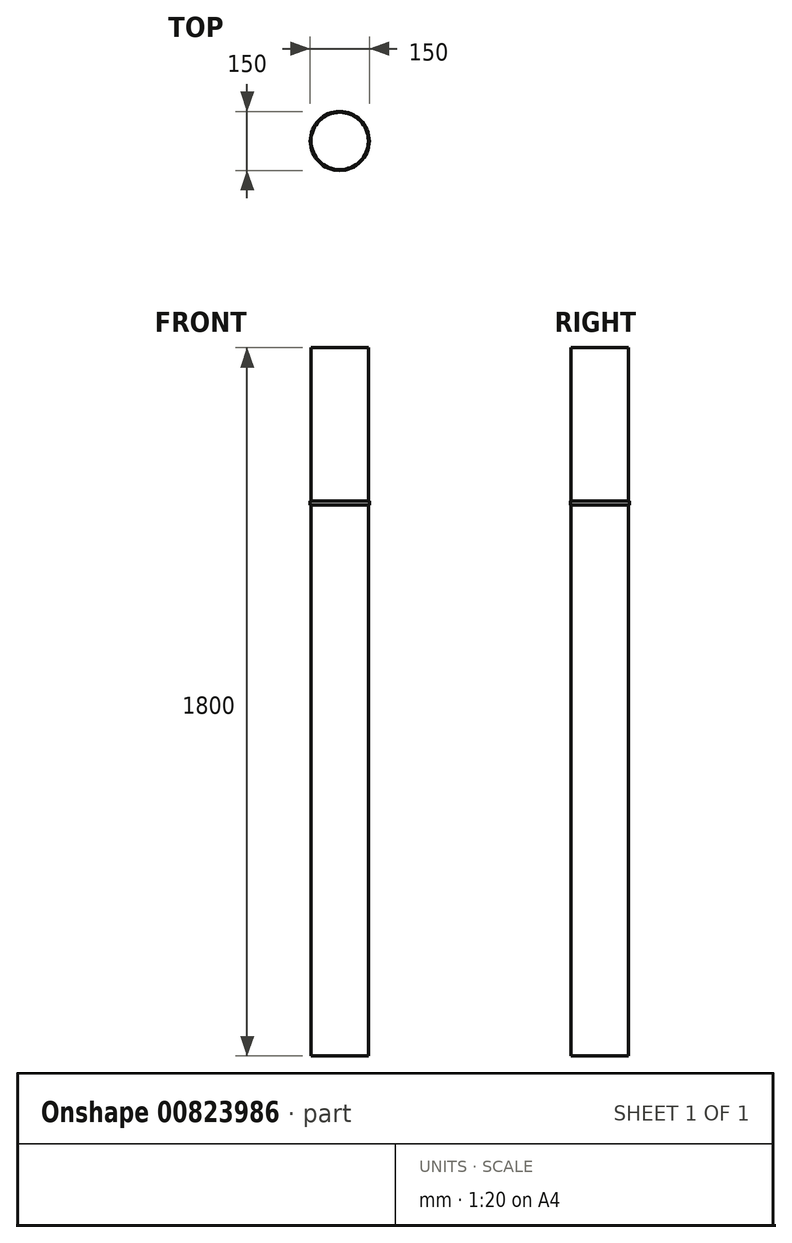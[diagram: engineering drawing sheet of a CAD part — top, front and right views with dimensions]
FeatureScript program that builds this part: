
annotation { "Feature Type Name" : "Feature", "Feature Type Description" : "" }
export const myFeature = defineFeature(function(context is Context, id is Id, definition is map)
    precondition{}
    {
        {
            var Q0;
            Q0=qCreatedBy(makeId("Top.planeOp"),FACE);
            var sketch = newSketch(context, id + "F0", { "sketchPlane" : qUnion([Q0])});
            skCircle(sketch, "E0", {"center": v(0, 0) * mm, "radius": 72.78 * mm});
            skSolve(sketch);
        }
        {
            var Q0;
            Q0=makeQuery(id+"F0.imprint","IMPRINT",FACE,{"disambiguationData":[TD([[makeQuery(id+"F0.imprint","IMPRINT",EDGE,{"derivedFrom":sQuery(id+"F0.wireOp",EDGE,"E0")}),1.0]])]});
            extrude(context, id + "F1", {"entities" : qUnion([Q0]), "depth" : 900 * mm, "offsetDistance" : 25 * mm, "hasSecondDirection" : true, "secondDirectionOppositeDirection" : true, "secondDirectionDepth" : 900 * mm});
        }
        {
            var Q0;
            Q0=qCreatedBy(makeId("Top.planeOp"),FACE);
            cPlane(context, id + "F2", {"entities" : qUnion([Q0]), "cplaneType" : CPlaneType.OFFSET, "offset" : 500 * mm, "width" : 150 * mm, "height" : 150 * mm});
        }
        {
            var Q0;
            Q0=qCreatedBy(id+"F2.planeOp",FACE);
            var sketch = newSketch(context, id + "F3", { "sketchPlane" : qUnion([Q0])});
            skCircle(sketch, "E1", {"center": v(0, 0) * mm, "radius": 75 * mm});
            skCircle(sketch, "E2.0", {"center": v(0, 0) * mm, "radius": 72.78 * mm});
            skSolve(sketch);
        }
        {
            var Q0;
            Q0 = qSketchRegion(id + "F3", true);
            extrude(context, id + "F4", {"entities" : qUnion([Q0]), "operationType" : NewBodyOperationType.ADD, "depth" : 10 * mm, "offsetDistance" : 25 * mm});
        }
    });
